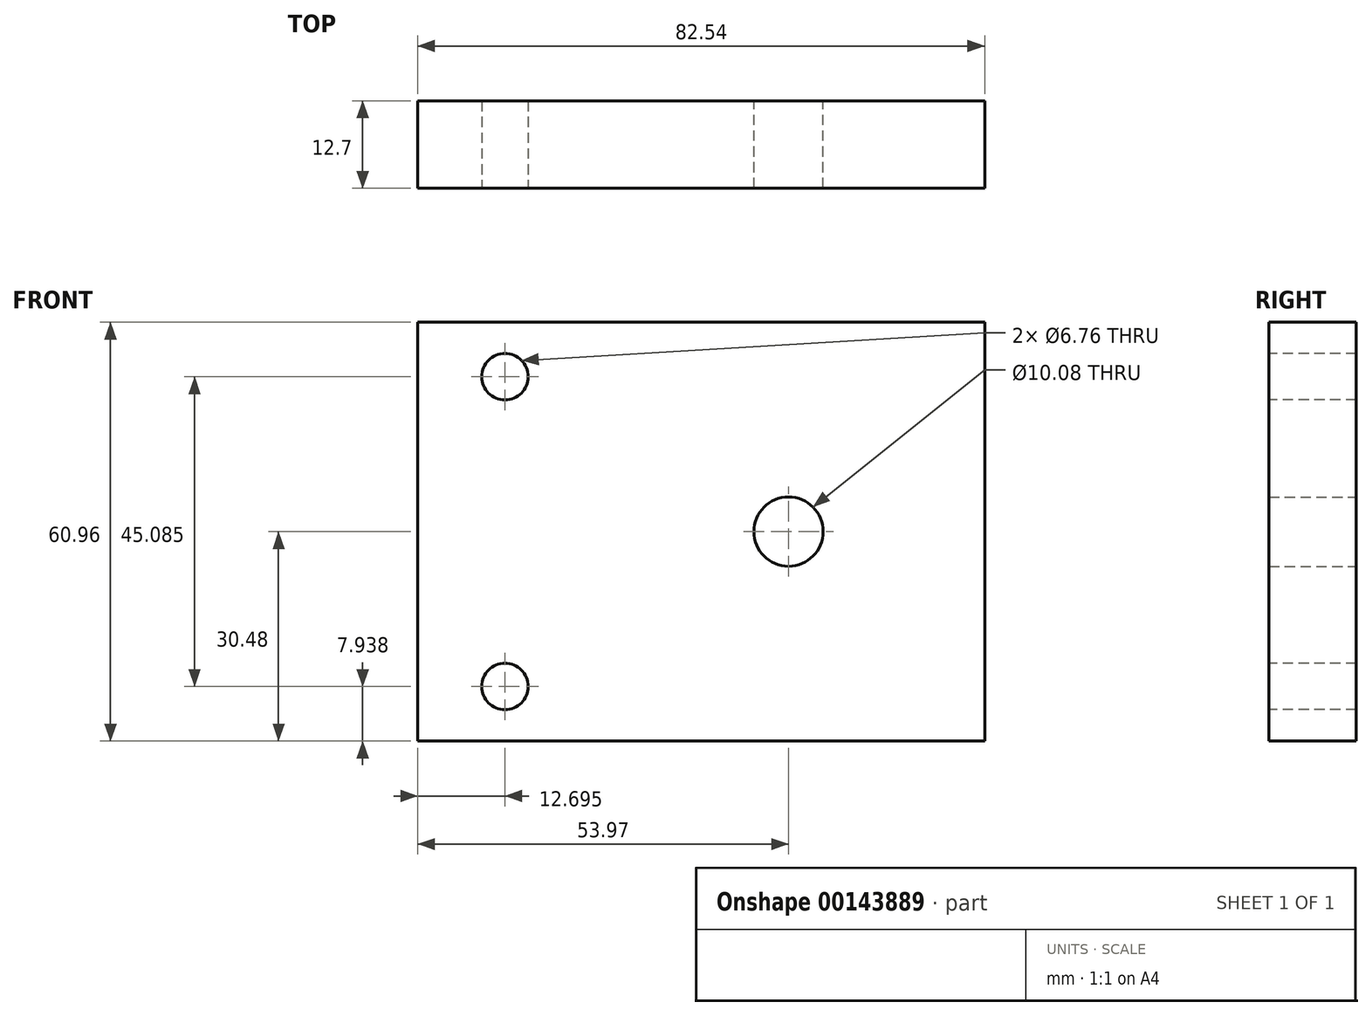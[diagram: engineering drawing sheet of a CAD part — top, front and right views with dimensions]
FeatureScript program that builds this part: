
annotation { "Feature Type Name" : "Feature", "Feature Type Description" : "" }
export const myFeature = defineFeature(function(context is Context, id is Id, definition is map)
    precondition{}
    {
        {
            var Q0;
            Q0=qCreatedBy(makeId("Front.planeOp"),FACE);
            var sketch = newSketch(context, id + "F0", { "sketchPlane" : qUnion([Q0])});
            skLineSegment(sketch, "E0.bottom", {"start": v(-41.28, 30.48) * mm, "end": v(41.28, 30.48) * mm});
            skLineSegment(sketch, "E0.top", {"start": v(-41.28, -30.48) * mm, "end": v(41.28, -30.48) * mm});
            skLineSegment(sketch, "E0.left", {"start": v(-41.28, 30.48) * mm, "end": v(-41.28, -30.48) * mm});
            skLineSegment(sketch, "E0.right", {"start": v(41.28, 30.48) * mm, "end": v(41.28, -30.48) * mm});
            skSolve(sketch);
        }
        {
            var Q0;
            Q0=makeQuery(id+"F0.imprint","IMPRINT",FACE,{"disambiguationData":[TD([[makeQuery(id+"F0.imprint","IMPRINT",EDGE,{"derivedFrom":sQuery(id+"F0.wireOp",EDGE,"E0.bottom")}),-1.0]])]});
            extrude(context, id + "F1", {"entities" : qUnion([Q0]), "depth" : 12.7 * mm});
        }
        {
            var Q0;
            Q0=makeQuery(id+"F1.opExtrude","CAP_FACE",FACE,{"disambiguationData":[OSD([sQuery(id+"F0.wireOp",EDGE,"E0.bottom"),sQuery(id+"F0.wireOp",EDGE,"E0.top"),sQuery(id+"F0.wireOp",EDGE,"E0.left"),sQuery(id+"F0.wireOp",EDGE,"E0.right")])],"isStart":true});
            var sketch = newSketch(context, id + "F2", { "sketchPlane" : qUnion([Q0])});
            skPoint(sketch, "E1", {"position": v(-12.7, 0) * mm});
            skSolve(sketch);
        }
        {
            var Q0;
            Q0=sQuery(id+"F2.wireOp",VERTEX,"E1");
            var Q1;
            Q1=makeQuery(id+"F1.opExtrude","SWEPT_BODY",BODY,{"disambiguationData":[OSD([sQuery(id+"F0.wireOp",EDGE,"E0.bottom"),sQuery(id+"F0.wireOp",EDGE,"E0.top"),sQuery(id+"F0.wireOp",EDGE,"E0.left"),sQuery(id+"F0.wireOp",EDGE,"E0.right")])]});
            hole(context, id + "F3", {"style" : HoleStyle.SIMPLE, "endStyle" : HoleEndStyle.THROUGH, "standardTappedOrClearance" : lookupTablePath({ "standard" : "ANSI", "fit" : "Normal (ASME)", "size" : "3/8", "type" : "Clearance" }), "standardBlindInLast" : lookupTablePath({ "fit" : "Free", "standard" : "ANSI", "size" : "3/8", "type" : "Clearance" }), "holeDiameter" : 10.08 * mm, "locations" : qUnion([Q0]), "scope" : qUnion([Q1]), "isTappedThrough" : true});
        }
        {
            var Q0;
            Q0=makeQuery(id+"F1.opExtrude","CAP_FACE",FACE,{"disambiguationData":[OSD([sQuery(id+"F0.wireOp",EDGE,"E0.bottom"),sQuery(id+"F0.wireOp",EDGE,"E0.top"),sQuery(id+"F0.wireOp",EDGE,"E0.left"),sQuery(id+"F0.wireOp",EDGE,"E0.right")])],"isStart":false});
            var sketch = newSketch(context, id + "F4", { "sketchPlane" : qUnion([Q0])});
            skPoint(sketch, "E2", {"position": v(-28.58, 22.54) * mm});
            skPoint(sketch, "E3", {"position": v(-28.58, -22.54) * mm});
            skSolve(sketch);
        }
        {
            var Q0;
            Q0=sQuery(id+"F4.wireOp",VERTEX,"E2");
            var Q1;
            Q1=sQuery(id+"F4.wireOp",VERTEX,"E3");
            var Q2;
            Q2=makeQuery(id+"F1.opExtrude","SWEPT_BODY",BODY,{"disambiguationData":[OSD([sQuery(id+"F0.wireOp",EDGE,"E0.bottom"),sQuery(id+"F0.wireOp",EDGE,"E0.top"),sQuery(id+"F0.wireOp",EDGE,"E0.left"),sQuery(id+"F0.wireOp",EDGE,"E0.right")])]});
            hole(context, id + "F5", {"style" : HoleStyle.SIMPLE, "endStyle" : HoleEndStyle.THROUGH, "standardTappedOrClearance" : lookupTablePath({ "standard" : "ANSI", "fit" : "Normal (ASME)", "size" : "1/4", "type" : "Clearance" }), "standardBlindInLast" : lookupTablePath({ "fit" : "Free", "standard" : "ANSI", "size" : "1/4", "type" : "Clearance" }), "holeDiameter" : 6.76 * mm, "locations" : qUnion([Q0, Q1]), "scope" : qUnion([Q2]), "isTappedThrough" : true});
        }
    });
